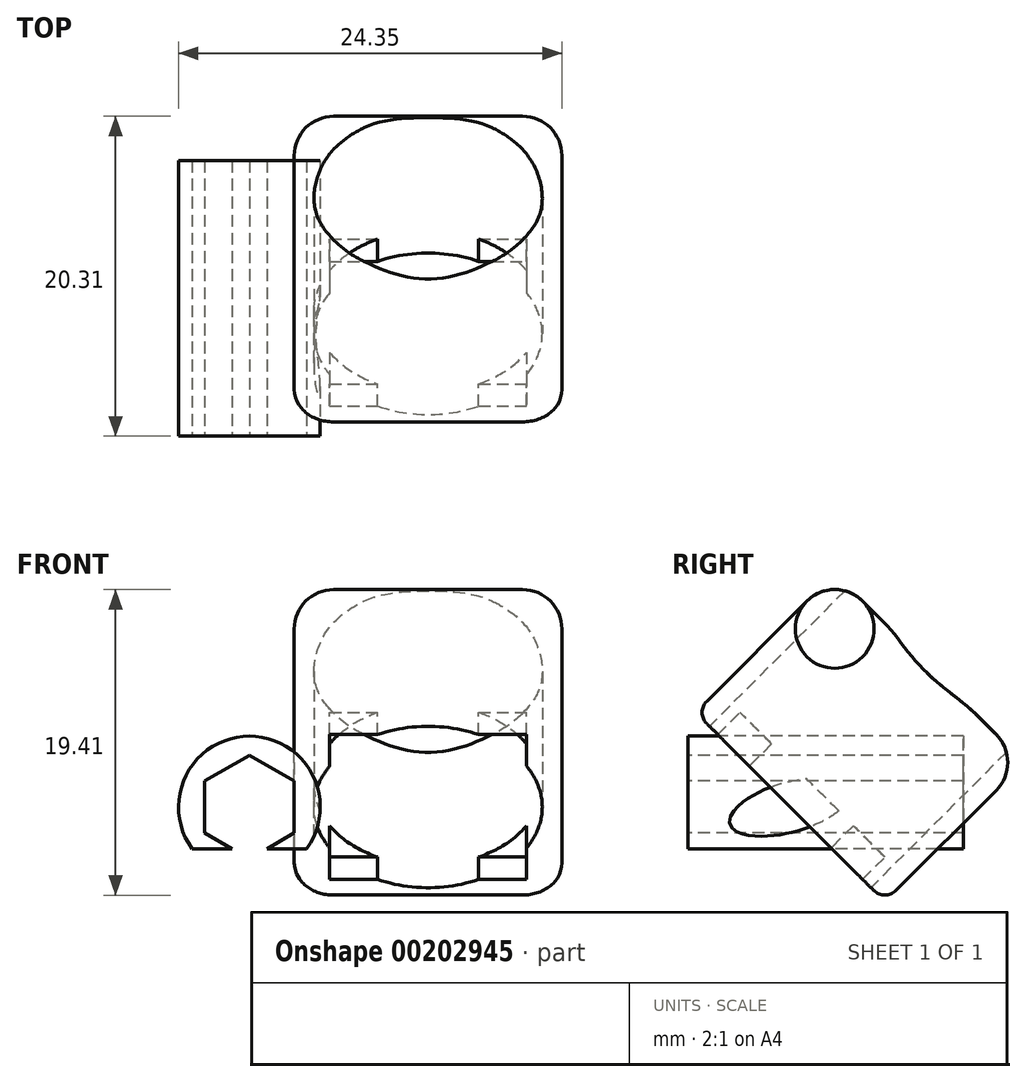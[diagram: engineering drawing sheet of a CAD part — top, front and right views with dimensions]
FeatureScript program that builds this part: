
annotation { "Feature Type Name" : "Feature", "Feature Type Description" : "" }
export const myFeature = defineFeature(function(context is Context, id is Id, definition is map)
    precondition{}
    {
        {
            var Q0;
            Q0=qCreatedBy(makeId("Top.planeOp"),FACE);
            var sketch = newSketch(context, id + "F0", { "sketchPlane" : qUnion([Q0])});
            skLineSegment(sketch, "E0.bottom", {"start": v(6.25, 6.25) * mm, "end": v(-6.25, 6.25) * mm});
            skLineSegment(sketch, "E0.top", {"start": v(6.25, -6.25) * mm, "end": v(-6.25, -6.25) * mm});
            skLineSegment(sketch, "E0.left", {"start": v(6.25, 6.25) * mm, "end": v(6.25, -6.25) * mm});
            skLineSegment(sketch, "E0.right", {"start": v(-6.25, 6.25) * mm, "end": v(-6.25, -6.25) * mm});
            skPoint(sketch, "E0.middle", {"position": v(0, 0) * mm});
            skCircle(sketch, "E1", {"center": v(0, 0) * mm, "radius": 7.25 * mm});
            skLineSegment(sketch, "E2.bottom", {"start": v(8.5, 8.5) * mm, "end": v(-8.5, 8.5) * mm});
            skLineSegment(sketch, "E2.top", {"start": v(8.5, -8.5) * mm, "end": v(-8.5, -8.5) * mm});
            skLineSegment(sketch, "E2.left", {"start": v(8.5, 8.5) * mm, "end": v(8.5, -8.5) * mm});
            skLineSegment(sketch, "E2.right", {"start": v(-8.5, 8.5) * mm, "end": v(-8.5, -8.5) * mm});
            skSolve(sketch);
        }
        {
            var Q0;
            Q0=makeQuery(id+"F0.imprint","IMPRINT",FACE,{"disambiguationData":[TD([[makeQuery(id+"F0.imprint","IMPRINT",EDGE,{"derivedFrom":sQuery(id+"F0.wireOp",EDGE,"E2.bottom")}),1.0]])]});
            var Q1;
            {var subQ0=sQuery(id+"F0.wireOp",EDGE,"E0.right");var subQ1=sQuery(id+"F0.wireOp",EDGE,"E0.bottom");var subQ2=makeQuery(id+"F0.imprint","INTERSECT",VERTEX,{"derivedFrom":[subQ1,subQ0]});Q1=makeQuery(id+"F0.imprint","IMPRINT",FACE,{"disambiguationData":[TD([[makeQuery(id+"F0.imprint","IMPRINT",EDGE,{"disambiguationData":[TD([[subQ2,1.0]])],"derivedFrom":subQ1}),1.0]])]});}
            var Q2;
            {var subQ0=sQuery(id+"F0.wireOp",EDGE,"E1");var subQ1=makeQuery(id+"F0.imprint","INTERSECT",VERTEX,{"derivedFrom":[sQuery(id+"F0.wireOp",EDGE,"E0.bottom"),subQ0]});Q2=makeQuery(id+"F0.imprint","IMPRINT",FACE,{"disambiguationData":[TD([[makeQuery(id+"F0.imprint","IMPRINT",EDGE,{"disambiguationData":[TD([[subQ1,1.0]])],"derivedFrom":subQ0}),1.0]])]});}
            var Q3;
            {var subQ0=sQuery(id+"F0.wireOp",EDGE,"E0.left");var subQ1=sQuery(id+"F0.wireOp",EDGE,"E0.bottom");var subQ2=makeQuery(id+"F0.imprint","INTERSECT",VERTEX,{"derivedFrom":[subQ1,subQ0]});Q3=makeQuery(id+"F0.imprint","IMPRINT",FACE,{"disambiguationData":[TD([[makeQuery(id+"F0.imprint","IMPRINT",EDGE,{"disambiguationData":[TD([[subQ2,-1.0]])],"derivedFrom":subQ1}),1.0]])]});}
            var Q4;
            {var subQ0=sQuery(id+"F0.wireOp",EDGE,"E0.left");var subQ1=sQuery(id+"F0.wireOp",EDGE,"E0.top");var subQ2=makeQuery(id+"F0.imprint","INTERSECT",VERTEX,{"derivedFrom":[subQ1,subQ0]});Q4=makeQuery(id+"F0.imprint","IMPRINT",FACE,{"disambiguationData":[TD([[makeQuery(id+"F0.imprint","IMPRINT",EDGE,{"disambiguationData":[TD([[subQ2,-1.0]])],"derivedFrom":subQ1}),-1.0]])]});}
            var Q5;
            {var subQ0=sQuery(id+"F0.wireOp",EDGE,"E0.right");var subQ1=sQuery(id+"F0.wireOp",EDGE,"E0.top");var subQ2=makeQuery(id+"F0.imprint","INTERSECT",VERTEX,{"derivedFrom":[subQ1,subQ0]});Q5=makeQuery(id+"F0.imprint","IMPRINT",FACE,{"disambiguationData":[TD([[makeQuery(id+"F0.imprint","IMPRINT",EDGE,{"disambiguationData":[TD([[subQ2,1.0]])],"derivedFrom":subQ1}),-1.0]])]});}
            extrude(context, id + "F1", {"entities" : qUnion([Q0, Q1, Q2, Q3, Q4, Q5]), "depth" : 12.5 * mm});
        }
        {
            var Q0;
            Q0=qCreatedBy(makeId("Top.planeOp"),FACE);
            var sketch = newSketch(context, id + "F2", { "sketchPlane" : qUnion([Q0])});
            skLineSegment(sketch, "E3", {"start": v(-15.14, 0) * mm, "end": v(14.33, 0) * mm});
            skSolve(sketch);
        }
        {
            var Q0;
            Q0=qCreatedBy(makeId("Front.planeOp"),FACE);
            var sketch = newSketch(context, id + "F3", { "sketchPlane" : qUnion([Q0])});
            skCircle(sketch, "E4", {"center": v(-11.35, 0) * mm, "radius": 4.5 * mm});
            skCircle(sketch, "E5.cCircle", {"center": v(-11.35, 0) * mm, "radius": 2.85 * mm, "construction": true});
            skLineSegment(sketch, "E5.0", {"start": v(-8.5, 1.65) * mm, "end": v(-8.5, -1.65) * mm});
            skLineSegment(sketch, "E5.1", {"start": v(-8.5, -1.65) * mm, "end": v(-11.35, -3.3) * mm});
            skLineSegment(sketch, "E5.2", {"start": v(-11.35, -3.3) * mm, "end": v(-14.2, -1.65) * mm});
            skLineSegment(sketch, "E5.3", {"start": v(-14.2, -1.65) * mm, "end": v(-14.2, 1.65) * mm});
            skLineSegment(sketch, "E5.4", {"start": v(-14.2, 1.65) * mm, "end": v(-11.35, 3.3) * mm});
            skLineSegment(sketch, "E5.5", {"start": v(-11.35, 3.3) * mm, "end": v(-8.5, 1.65) * mm});
            skPoint(sketch, "E5.0.midPoint", {"position": v(-8.5, 0) * mm});
            skPoint(sketch, "E6.visualSharp", {"position": v(20, -23.1) * mm});
            skArc(sketch, "E7", {"start": v(3.92, -36.51) * mm, "mid": v(1.52, -37.5) * mm, "end": v(0.52, -39.91) * mm});
            skArc(sketch, "E8", {"start": v(0.52, -39.91) * mm, "mid": v(1.52, -42.32) * mm, "end": v(3.92, -43.31) * mm});
            skArc(sketch, "E9", {"start": v(3.92, -43.31) * mm, "mid": v(6.32, -42.32) * mm, "end": v(7.32, -39.91) * mm});
            skArc(sketch, "E10", {"start": v(7.32, -39.91) * mm, "mid": v(6.32, -37.5) * mm, "end": v(3.92, -36.51) * mm});
            skLineSegment(sketch, "E11", {"start": v(13.47, -32.4) * mm, "end": v(14.37, -29.02) * mm});
            skArc(sketch, "E12", {"start": v(14.37, -29.02) * mm, "mid": v(14.86, -28.38) * mm, "end": v(15.66, -28.28) * mm});
            skArc(sketch, "E13", {"start": v(15.66, -28.28) * mm, "mid": v(16.3, -28.77) * mm, "end": v(16.4, -29.56) * mm});
            skLineSegment(sketch, "E14", {"start": v(16.4, -29.56) * mm, "end": v(15.5, -32.94) * mm});
            skArc(sketch, "E15", {"start": v(15.5, -32.94) * mm, "mid": v(15, -33.58) * mm, "end": v(14.2, -33.69) * mm});
            skArc(sketch, "E16", {"start": v(14.2, -33.69) * mm, "mid": v(13.57, -33.2) * mm, "end": v(13.47, -32.4) * mm});
            skLineSegment(sketch, "E17", {"start": v(4.42, -34.66) * mm, "end": v(4.44, -34.66) * mm});
            skArc(sketch, "E18", {"start": v(4.44, -34.66) * mm, "mid": v(5.22, -34.2) * mm, "end": v(5.2, -33.28) * mm});
            skLineSegment(sketch, "E19", {"start": v(5.2, -33.28) * mm, "end": v(4.72, -32.52) * mm});
            skLineSegment(sketch, "E20", {"start": v(4.72, -32.52) * mm, "end": v(4.37, -31.96) * mm});
            skLineSegment(sketch, "E21", {"start": v(4.37, -31.96) * mm, "end": v(4.37, -31.94) * mm});
            skLineSegment(sketch, "E22", {"start": v(4.37, -31.94) * mm, "end": v(4.6, -31.62) * mm});
            skLineSegment(sketch, "E23", {"start": v(4.6, -31.62) * mm, "end": v(4.94, -31.07) * mm});
            skLineSegment(sketch, "E24", {"start": v(4.94, -31.07) * mm, "end": v(5.24, -30.47) * mm});
            skLineSegment(sketch, "E25", {"start": v(5.24, -30.47) * mm, "end": v(5.32, -30.27) * mm});
            skLineSegment(sketch, "E26", {"start": v(5.32, -30.27) * mm, "end": v(5.34, -30.22) * mm});
            skLineSegment(sketch, "E27", {"start": v(5.34, -30.22) * mm, "end": v(5.36, -30.18) * mm});
            skLineSegment(sketch, "E28", {"start": v(5.36, -30.18) * mm, "end": v(5.5, -29.83) * mm});
            skLineSegment(sketch, "E29", {"start": v(5.5, -29.83) * mm, "end": v(5.61, -29.45) * mm});
            skLineSegment(sketch, "E30", {"start": v(5.61, -29.45) * mm, "end": v(5.72, -29.07) * mm});
            skLineSegment(sketch, "E31", {"start": v(5.72, -29.07) * mm, "end": v(5.8, -28.68) * mm});
            skLineSegment(sketch, "E32", {"start": v(5.8, -28.68) * mm, "end": v(5.87, -28.28) * mm});
            skLineSegment(sketch, "E33", {"start": v(5.87, -28.28) * mm, "end": v(5.92, -27.87) * mm});
            skLineSegment(sketch, "E34", {"start": v(5.92, -27.87) * mm, "end": v(5.95, -27.45) * mm});
            skLineSegment(sketch, "E35", {"start": v(5.95, -27.45) * mm, "end": v(5.96, -27.03) * mm});
            skLineSegment(sketch, "E36", {"start": v(5.96, -27.03) * mm, "end": v(5.95, -26.6) * mm});
            skLineSegment(sketch, "E37", {"start": v(5.95, -26.6) * mm, "end": v(5.92, -26.2) * mm});
            skLineSegment(sketch, "E38", {"start": v(5.92, -26.2) * mm, "end": v(5.87, -25.79) * mm});
            skLineSegment(sketch, "E39", {"start": v(5.87, -25.79) * mm, "end": v(5.8, -25.39) * mm});
            skLineSegment(sketch, "E40", {"start": v(5.8, -25.39) * mm, "end": v(5.72, -25) * mm});
            skLineSegment(sketch, "E41", {"start": v(5.72, -25) * mm, "end": v(5.61, -24.61) * mm});
            skLineSegment(sketch, "E42", {"start": v(5.61, -24.61) * mm, "end": v(5.5, -24.24) * mm});
            skLineSegment(sketch, "E43", {"start": v(5.5, -24.24) * mm, "end": v(5.36, -23.88) * mm});
            skLineSegment(sketch, "E44", {"start": v(5.36, -23.88) * mm, "end": v(5.34, -23.84) * mm});
            skLineSegment(sketch, "E45", {"start": v(5.34, -23.84) * mm, "end": v(5.32, -23.8) * mm});
            skLineSegment(sketch, "E46", {"start": v(5.32, -23.8) * mm, "end": v(5.24, -23.6) * mm});
            skLineSegment(sketch, "E47", {"start": v(5.24, -23.6) * mm, "end": v(4.94, -23) * mm});
            skLineSegment(sketch, "E48", {"start": v(4.94, -23) * mm, "end": v(4.6, -22.44) * mm});
            skLineSegment(sketch, "E49", {"start": v(4.6, -22.44) * mm, "end": v(4.37, -22.12) * mm});
            skLineSegment(sketch, "E50", {"start": v(4.37, -22.12) * mm, "end": v(4.37, -22.1) * mm});
            skLineSegment(sketch, "E51", {"start": v(4.37, -22.1) * mm, "end": v(4.72, -21.54) * mm});
            skLineSegment(sketch, "E52", {"start": v(4.72, -21.54) * mm, "end": v(5.2, -20.78) * mm});
            skArc(sketch, "E53", {"start": v(5.2, -20.78) * mm, "mid": v(5.22, -19.87) * mm, "end": v(4.44, -19.4) * mm});
            skLineSegment(sketch, "E54", {"start": v(4.44, -19.4) * mm, "end": v(3.9, -19.4) * mm});
            skArc(sketch, "E55", {"start": v(3.9, -19.4) * mm, "mid": v(3.47, -19.52) * mm, "end": v(3.15, -19.82) * mm});
            skLineSegment(sketch, "E56", {"start": v(3.15, -19.82) * mm, "end": v(2.68, -20.58) * mm});
            skLineSegment(sketch, "E57", {"start": v(2.68, -20.58) * mm, "end": v(2.37, -20.4) * mm});
            skLineSegment(sketch, "E58", {"start": v(2.37, -20.4) * mm, "end": v(2.06, -20.25) * mm});
            skLineSegment(sketch, "E59", {"start": v(2.06, -20.25) * mm, "end": v(1.74, -20.12) * mm});
            skLineSegment(sketch, "E60", {"start": v(1.74, -20.12) * mm, "end": v(1.41, -20.01) * mm});
            skLineSegment(sketch, "E61", {"start": v(1.41, -20.01) * mm, "end": v(1.08, -19.93) * mm});
            skLineSegment(sketch, "E62", {"start": v(1.08, -19.93) * mm, "end": v(0.73, -19.86) * mm});
            skLineSegment(sketch, "E63", {"start": v(0.73, -19.86) * mm, "end": v(0.38, -19.83) * mm});
            skLineSegment(sketch, "E64", {"start": v(0.38, -19.83) * mm, "end": v(0.03, -19.81) * mm});
            skLineSegment(sketch, "E65", {"start": v(0.03, -19.81) * mm, "end": v(-0.04, -19.82) * mm});
            skLineSegment(sketch, "E66", {"start": v(-0.04, -19.82) * mm, "end": v(-0.11, -19.81) * mm});
            skLineSegment(sketch, "E67", {"start": v(-0.11, -19.81) * mm, "end": v(-0.46, -19.83) * mm});
            skLineSegment(sketch, "E68", {"start": v(-0.46, -19.83) * mm, "end": v(-0.8, -19.86) * mm});
            skLineSegment(sketch, "E69", {"start": v(-0.8, -19.86) * mm, "end": v(-1.15, -19.92) * mm});
            skLineSegment(sketch, "E70", {"start": v(-1.15, -19.92) * mm, "end": v(-1.48, -20) * mm});
            skLineSegment(sketch, "E71", {"start": v(-1.48, -20) * mm, "end": v(-1.8, -20.11) * mm});
            skLineSegment(sketch, "E72", {"start": v(-1.8, -20.11) * mm, "end": v(-2.12, -20.24) * mm});
            skLineSegment(sketch, "E73", {"start": v(-2.12, -20.24) * mm, "end": v(-2.43, -20.39) * mm});
            skLineSegment(sketch, "E74", {"start": v(-2.43, -20.39) * mm, "end": v(-2.73, -20.56) * mm});
            skLineSegment(sketch, "E75", {"start": v(-2.73, -20.56) * mm, "end": v(-2.98, -20.21) * mm});
            skLineSegment(sketch, "E76", {"start": v(-2.98, -20.21) * mm, "end": v(-3.05, -20.11) * mm});
            skLineSegment(sketch, "E77", {"start": v(-3.05, -20.11) * mm, "end": v(-3.24, -19.82) * mm});
            skArc(sketch, "E78", {"start": v(-3.24, -19.82) * mm, "mid": v(-3.56, -19.52) * mm, "end": v(-4, -19.4) * mm});
            skLineSegment(sketch, "E79", {"start": v(-4, -19.4) * mm, "end": v(-4.52, -19.4) * mm});
            skArc(sketch, "E80", {"start": v(-4.52, -19.4) * mm, "mid": v(-5.31, -19.87) * mm, "end": v(-5.29, -20.78) * mm});
            skLineSegment(sketch, "E81", {"start": v(-5.29, -20.78) * mm, "end": v(-4.45, -22.11) * mm});
            skLineSegment(sketch, "E82", {"start": v(-4.45, -22.11) * mm, "end": v(-4.63, -22.36) * mm});
            skLineSegment(sketch, "E83", {"start": v(-4.63, -22.36) * mm, "end": v(-4.8, -22.61) * mm});
            skLineSegment(sketch, "E84", {"start": v(-4.8, -22.61) * mm, "end": v(-4.96, -22.88) * mm});
            skLineSegment(sketch, "E85", {"start": v(-4.96, -22.88) * mm, "end": v(-5.12, -23.16) * mm});
            skLineSegment(sketch, "E86", {"start": v(-5.12, -23.16) * mm, "end": v(-5.26, -23.44) * mm});
            skLineSegment(sketch, "E87", {"start": v(-5.26, -23.44) * mm, "end": v(-5.39, -23.73) * mm});
            skLineSegment(sketch, "E88", {"start": v(-5.39, -23.73) * mm, "end": v(-5.5, -24.03) * mm});
            skLineSegment(sketch, "E89", {"start": v(-5.5, -24.03) * mm, "end": v(-5.62, -24.34) * mm});
            skLineSegment(sketch, "E90", {"start": v(-5.62, -24.34) * mm, "end": v(-5.71, -24.66) * mm});
            skLineSegment(sketch, "E91", {"start": v(-5.71, -24.66) * mm, "end": v(-5.8, -24.98) * mm});
            skLineSegment(sketch, "E92", {"start": v(-5.8, -24.98) * mm, "end": v(-5.87, -25.3) * mm});
            skLineSegment(sketch, "E93", {"start": v(-5.87, -25.3) * mm, "end": v(-5.93, -25.64) * mm});
            skLineSegment(sketch, "E94", {"start": v(-5.93, -25.64) * mm, "end": v(-5.98, -25.98) * mm});
            skLineSegment(sketch, "E95", {"start": v(-5.98, -25.98) * mm, "end": v(-6.02, -26.33) * mm});
            skLineSegment(sketch, "E96", {"start": v(-6.02, -26.33) * mm, "end": v(-6.04, -26.68) * mm});
            skLineSegment(sketch, "E97", {"start": v(-6.04, -26.68) * mm, "end": v(-6.04, -27.03) * mm});
            skLineSegment(sketch, "E98", {"start": v(-6.04, -27.03) * mm, "end": v(-6.04, -27.39) * mm});
            skLineSegment(sketch, "E99", {"start": v(-6.04, -27.39) * mm, "end": v(-6.02, -27.74) * mm});
            skLineSegment(sketch, "E100", {"start": v(-6.02, -27.74) * mm, "end": v(-5.98, -28.08) * mm});
            skLineSegment(sketch, "E101", {"start": v(-5.98, -28.08) * mm, "end": v(-5.93, -28.42) * mm});
            skLineSegment(sketch, "E102", {"start": v(-5.93, -28.42) * mm, "end": v(-5.87, -28.76) * mm});
            skLineSegment(sketch, "E103", {"start": v(-5.87, -28.76) * mm, "end": v(-5.8, -29.08) * mm});
            skLineSegment(sketch, "E104", {"start": v(-5.8, -29.08) * mm, "end": v(-5.71, -29.4) * mm});
            skLineSegment(sketch, "E105", {"start": v(-5.71, -29.4) * mm, "end": v(-5.62, -29.72) * mm});
            skLineSegment(sketch, "E106", {"start": v(-5.62, -29.72) * mm, "end": v(-5.5, -30.03) * mm});
            skLineSegment(sketch, "E107", {"start": v(-5.5, -30.03) * mm, "end": v(-5.39, -30.33) * mm});
            skLineSegment(sketch, "E108", {"start": v(-5.39, -30.33) * mm, "end": v(-5.26, -30.62) * mm});
            skLineSegment(sketch, "E109", {"start": v(-5.26, -30.62) * mm, "end": v(-5.12, -30.9) * mm});
            skLineSegment(sketch, "E110", {"start": v(-5.12, -30.9) * mm, "end": v(-4.96, -31.18) * mm});
            skLineSegment(sketch, "E111", {"start": v(-4.96, -31.18) * mm, "end": v(-4.8, -31.45) * mm});
            skLineSegment(sketch, "E112", {"start": v(-4.8, -31.45) * mm, "end": v(-4.63, -31.7) * mm});
            skLineSegment(sketch, "E113", {"start": v(-4.63, -31.7) * mm, "end": v(-4.45, -31.95) * mm});
            skLineSegment(sketch, "E114", {"start": v(-4.45, -31.95) * mm, "end": v(-5.29, -33.28) * mm});
            skArc(sketch, "E115", {"start": v(-5.29, -33.28) * mm, "mid": v(-5.31, -34.2) * mm, "end": v(-4.52, -34.66) * mm});
            skLineSegment(sketch, "E116", {"start": v(-4.52, -34.66) * mm, "end": v(-4.44, -34.66) * mm});
            skLineSegment(sketch, "E117", {"start": v(-4.44, -34.66) * mm, "end": v(-4.36, -34.66) * mm});
            skLineSegment(sketch, "E118", {"start": v(-4.36, -34.66) * mm, "end": v(-4, -34.66) * mm});
            skArc(sketch, "E119", {"start": v(-4, -34.66) * mm, "mid": v(-3.56, -34.55) * mm, "end": v(-3.24, -34.24) * mm});
            skLineSegment(sketch, "E120", {"start": v(-3.24, -34.24) * mm, "end": v(-3.05, -33.95) * mm});
            skLineSegment(sketch, "E121", {"start": v(-3.05, -33.95) * mm, "end": v(-2.98, -33.85) * mm});
            skLineSegment(sketch, "E122", {"start": v(-2.98, -33.85) * mm, "end": v(-2.73, -33.5) * mm});
            skLineSegment(sketch, "E123", {"start": v(-2.73, -33.5) * mm, "end": v(-2.43, -33.68) * mm});
            skLineSegment(sketch, "E124", {"start": v(-2.43, -33.68) * mm, "end": v(-2.12, -33.82) * mm});
            skLineSegment(sketch, "E125", {"start": v(-2.12, -33.82) * mm, "end": v(-1.8, -33.95) * mm});
            skLineSegment(sketch, "E126", {"start": v(-1.8, -33.95) * mm, "end": v(-1.48, -34.06) * mm});
            skLineSegment(sketch, "E127", {"start": v(-1.48, -34.06) * mm, "end": v(-1.15, -34.14) * mm});
            skLineSegment(sketch, "E128", {"start": v(-1.15, -34.14) * mm, "end": v(-0.8, -34.2) * mm});
            skLineSegment(sketch, "E129", {"start": v(-0.8, -34.2) * mm, "end": v(-0.46, -34.24) * mm});
            skLineSegment(sketch, "E130", {"start": v(-0.46, -34.24) * mm, "end": v(-0.11, -34.25) * mm});
            skLineSegment(sketch, "E131", {"start": v(-0.11, -34.25) * mm, "end": v(-0.06, -34.25) * mm});
            skLineSegment(sketch, "E132", {"start": v(-0.06, -34.25) * mm, "end": v(0.03, -34.25) * mm});
            skLineSegment(sketch, "E133", {"start": v(0.03, -34.25) * mm, "end": v(0.38, -34.24) * mm});
            skLineSegment(sketch, "E134", {"start": v(0.38, -34.24) * mm, "end": v(0.73, -34.2) * mm});
            skLineSegment(sketch, "E135", {"start": v(0.73, -34.2) * mm, "end": v(1.08, -34.14) * mm});
            skLineSegment(sketch, "E136", {"start": v(1.08, -34.14) * mm, "end": v(1.41, -34.05) * mm});
            skLineSegment(sketch, "E137", {"start": v(1.41, -34.05) * mm, "end": v(1.74, -33.94) * mm});
            skLineSegment(sketch, "E138", {"start": v(1.74, -33.94) * mm, "end": v(2.06, -33.8) * mm});
            skLineSegment(sketch, "E139", {"start": v(2.06, -33.8) * mm, "end": v(2.37, -33.66) * mm});
            skLineSegment(sketch, "E140", {"start": v(2.37, -33.66) * mm, "end": v(2.68, -33.48) * mm});
            skLineSegment(sketch, "E141", {"start": v(2.68, -33.48) * mm, "end": v(3.15, -34.24) * mm});
            skArc(sketch, "E142", {"start": v(3.15, -34.24) * mm, "mid": v(3.47, -34.55) * mm, "end": v(3.9, -34.66) * mm});
            skLineSegment(sketch, "E143", {"start": v(3.9, -34.66) * mm, "end": v(4.42, -34.66) * mm});
            skLineSegment(sketch, "E144", {"start": v(-13.55, -32.4) * mm, "end": v(-14.46, -29.02) * mm});
            skArc(sketch, "E145", {"start": v(-14.46, -29.02) * mm, "mid": v(-14.95, -28.38) * mm, "end": v(-15.75, -28.28) * mm});
            skArc(sketch, "E146", {"start": v(-15.75, -28.28) * mm, "mid": v(-16.38, -28.77) * mm, "end": v(-16.49, -29.56) * mm});
            skLineSegment(sketch, "E147", {"start": v(-16.49, -29.56) * mm, "end": v(-15.58, -32.94) * mm});
            skArc(sketch, "E148", {"start": v(-15.58, -32.94) * mm, "mid": v(-15.1, -33.58) * mm, "end": v(-14.3, -33.69) * mm});
            skArc(sketch, "E149", {"start": v(-14.3, -33.69) * mm, "mid": v(-13.66, -33.2) * mm, "end": v(-13.55, -32.4) * mm});
            skLineSegment(sketch, "E150", {"start": v(15.57, 0.36) * mm, "end": v(15.63, 0.26) * mm});
            skLineSegment(sketch, "E151", {"start": v(15.66, 0.2) * mm, "end": v(16.02, -0.48) * mm});
            skLineSegment(sketch, "E152", {"start": v(16.05, -0.53) * mm, "end": v(16.4, -1.23) * mm});
            skLineSegment(sketch, "E153", {"start": v(16.42, -1.28) * mm, "end": v(16.74, -2) * mm});
            skLineSegment(sketch, "E154", {"start": v(16.76, -2.04) * mm, "end": v(17.06, -2.76) * mm});
            skLineSegment(sketch, "E155", {"start": v(17.08, -2.8) * mm, "end": v(17.37, -3.53) * mm});
            skLineSegment(sketch, "E156", {"start": v(17.38, -3.58) * mm, "end": v(17.65, -4.3) * mm});
            skLineSegment(sketch, "E157", {"start": v(17.66, -4.35) * mm, "end": v(17.9, -5.1) * mm});
            skLineSegment(sketch, "E158", {"start": v(17.92, -5.13) * mm, "end": v(18.15, -5.88) * mm});
            skLineSegment(sketch, "E159", {"start": v(18.16, -5.92) * mm, "end": v(18.37, -6.67) * mm});
            skLineSegment(sketch, "E160", {"start": v(18.38, -6.7) * mm, "end": v(18.58, -7.46) * mm});
            skLineSegment(sketch, "E161", {"start": v(18.59, -7.5) * mm, "end": v(18.77, -8.25) * mm});
            skLineSegment(sketch, "E162", {"start": v(18.78, -8.28) * mm, "end": v(18.94, -9.04) * mm});
            skLineSegment(sketch, "E163", {"start": v(18.95, -9.07) * mm, "end": v(19.1, -9.83) * mm});
            skLineSegment(sketch, "E164", {"start": v(19.1, -9.86) * mm, "end": v(19.24, -10.62) * mm});
            skLineSegment(sketch, "E165", {"start": v(19.24, -10.65) * mm, "end": v(19.37, -11.4) * mm});
            skLineSegment(sketch, "E166", {"start": v(19.37, -11.44) * mm, "end": v(19.48, -12.2) * mm});
            skLineSegment(sketch, "E167", {"start": v(19.48, -12.22) * mm, "end": v(19.58, -12.98) * mm});
            skLineSegment(sketch, "E168", {"start": v(19.58, -13) * mm, "end": v(19.67, -13.76) * mm});
            skLineSegment(sketch, "E169", {"start": v(19.67, -13.78) * mm, "end": v(19.74, -14.53) * mm});
            skLineSegment(sketch, "E170", {"start": v(19.75, -14.56) * mm, "end": v(19.81, -15.3) * mm});
            skLineSegment(sketch, "E171", {"start": v(19.81, -15.32) * mm, "end": v(19.87, -16.06) * mm});
            skLineSegment(sketch, "E172", {"start": v(19.87, -16.08) * mm, "end": v(19.91, -16.81) * mm});
            skLineSegment(sketch, "E173", {"start": v(19.91, -16.84) * mm, "end": v(19.95, -17.56) * mm});
            skLineSegment(sketch, "E174", {"start": v(19.95, -17.6) * mm, "end": v(20, -19.02) * mm});
            skLineSegment(sketch, "E175", {"start": v(20, -19.05) * mm, "end": v(20.02, -20.45) * mm});
            skLineSegment(sketch, "E176", {"start": v(20.02, -20.48) * mm, "end": v(20.02, -21.83) * mm});
            skLineSegment(sketch, "E177", {"start": v(20.02, -21.86) * mm, "end": v(20, -23.02) * mm});
            skLineSegment(sketch, "E178", {"start": v(20, -23.05) * mm, "end": v(19.95, -24.25) * mm});
            skLineSegment(sketch, "E179", {"start": v(19.95, -24.29) * mm, "end": v(19.88, -25.51) * mm});
            skLineSegment(sketch, "E180", {"start": v(19.88, -25.55) * mm, "end": v(19.83, -26.17) * mm});
            skLineSegment(sketch, "E181", {"start": v(19.83, -26.2) * mm, "end": v(19.77, -26.82) * mm});
            skLineSegment(sketch, "E182", {"start": v(19.77, -26.84) * mm, "end": v(19.7, -27.47) * mm});
            skLineSegment(sketch, "E183", {"start": v(19.7, -27.5) * mm, "end": v(19.64, -28.14) * mm});
            skLineSegment(sketch, "E184", {"start": v(19.63, -28.16) * mm, "end": v(19.55, -28.8) * mm});
            skLineSegment(sketch, "E185", {"start": v(19.55, -28.83) * mm, "end": v(19.46, -29.47) * mm});
            skLineSegment(sketch, "E186", {"start": v(19.45, -29.5) * mm, "end": v(19.35, -30.15) * mm});
            skLineSegment(sketch, "E187", {"start": v(19.35, -30.18) * mm, "end": v(19.24, -30.82) * mm});
            skLineSegment(sketch, "E188", {"start": v(19.23, -30.85) * mm, "end": v(19.1, -31.5) * mm});
            skLineSegment(sketch, "E189", {"start": v(19.1, -31.53) * mm, "end": v(18.97, -32.18) * mm});
            skLineSegment(sketch, "E190", {"start": v(18.96, -32.22) * mm, "end": v(18.81, -32.86) * mm});
            skLineSegment(sketch, "E191", {"start": v(18.8, -32.9) * mm, "end": v(18.65, -33.54) * mm});
            skLineSegment(sketch, "E192", {"start": v(18.64, -33.58) * mm, "end": v(18.47, -34.23) * mm});
            skLineSegment(sketch, "E193", {"start": v(18.46, -34.26) * mm, "end": v(18.27, -34.9) * mm});
            skLineSegment(sketch, "E194", {"start": v(18.26, -34.94) * mm, "end": v(18.06, -35.58) * mm});
            skLineSegment(sketch, "E195", {"start": v(18.05, -35.62) * mm, "end": v(17.83, -36.26) * mm});
            skLineSegment(sketch, "E196", {"start": v(17.82, -36.3) * mm, "end": v(17.6, -36.93) * mm});
            skLineSegment(sketch, "E197", {"start": v(17.57, -36.97) * mm, "end": v(17.33, -37.6) * mm});
            skLineSegment(sketch, "E198", {"start": v(17.31, -37.64) * mm, "end": v(17.05, -38.27) * mm});
            skLineSegment(sketch, "E199", {"start": v(17.04, -38.31) * mm, "end": v(16.76, -38.93) * mm});
            skLineSegment(sketch, "E200", {"start": v(16.74, -38.97) * mm, "end": v(16.45, -39.58) * mm});
            skLineSegment(sketch, "E201", {"start": v(16.42, -39.63) * mm, "end": v(16.11, -40.23) * mm});
            skLineSegment(sketch, "E202", {"start": v(16.09, -40.27) * mm, "end": v(15.76, -40.87) * mm});
            skLineSegment(sketch, "E203", {"start": v(15.73, -40.92) * mm, "end": v(15.48, -41.35) * mm});
            skLineSegment(sketch, "E204", {"start": v(8.6, -44.86) * mm, "end": v(2.96, -44.86) * mm});
            skLineSegment(sketch, "E205", {"start": v(2.96, -44.86) * mm, "end": v(-0.04, -44.86) * mm});
            skLineSegment(sketch, "E206", {"start": v(-0.04, -44.86) * mm, "end": v(-3.04, -44.86) * mm});
            skLineSegment(sketch, "E207", {"start": v(-3.04, -44.86) * mm, "end": v(-8.6, -44.86) * mm});
            skLineSegment(sketch, "E208", {"start": v(-15.74, -40.47) * mm, "end": v(-16.08, -39.89) * mm});
            skLineSegment(sketch, "E209", {"start": v(-16.08, -39.89) * mm, "end": v(-16.41, -39.3) * mm});
            skLineSegment(sketch, "E210", {"start": v(-16.41, -39.3) * mm, "end": v(-16.72, -38.7) * mm});
            skLineSegment(sketch, "E211", {"start": v(-16.72, -38.7) * mm, "end": v(-17.01, -38.09) * mm});
            skLineSegment(sketch, "E212", {"start": v(-17.01, -38.09) * mm, "end": v(-17.29, -37.47) * mm});
            skLineSegment(sketch, "E213", {"start": v(-17.29, -37.47) * mm, "end": v(-17.55, -36.85) * mm});
            skLineSegment(sketch, "E214", {"start": v(-17.55, -36.85) * mm, "end": v(-17.79, -36.22) * mm});
            skLineSegment(sketch, "E215", {"start": v(-17.79, -36.22) * mm, "end": v(-18.02, -35.6) * mm});
            skLineSegment(sketch, "E216", {"start": v(-18.02, -35.6) * mm, "end": v(-18.23, -34.96) * mm});
            skLineSegment(sketch, "E217", {"start": v(-18.23, -34.96) * mm, "end": v(-18.43, -34.32) * mm});
            skLineSegment(sketch, "E218", {"start": v(-18.43, -34.32) * mm, "end": v(-18.61, -33.67) * mm});
            skLineSegment(sketch, "E219", {"start": v(-18.61, -33.67) * mm, "end": v(-18.79, -33.03) * mm});
            skLineSegment(sketch, "E220", {"start": v(-18.79, -33.03) * mm, "end": v(-18.95, -32.38) * mm});
            skLineSegment(sketch, "E221", {"start": v(-18.95, -32.38) * mm, "end": v(-19.1, -31.73) * mm});
            skLineSegment(sketch, "E222", {"start": v(-19.1, -31.73) * mm, "end": v(-19.23, -31.09) * mm});
            skLineSegment(sketch, "E223", {"start": v(-19.23, -31.09) * mm, "end": v(-19.35, -30.44) * mm});
            skLineSegment(sketch, "E224", {"start": v(-19.35, -30.44) * mm, "end": v(-19.46, -29.8) * mm});
            skLineSegment(sketch, "E225", {"start": v(-19.46, -29.8) * mm, "end": v(-19.56, -29.15) * mm});
            skLineSegment(sketch, "E226", {"start": v(-19.56, -29.15) * mm, "end": v(-19.65, -28.5) * mm});
            skLineSegment(sketch, "E227", {"start": v(-19.65, -28.5) * mm, "end": v(-19.73, -27.86) * mm});
            skLineSegment(sketch, "E228", {"start": v(-19.73, -27.86) * mm, "end": v(-19.8, -27.22) * mm});
            skLineSegment(sketch, "E229", {"start": v(-19.8, -27.22) * mm, "end": v(-19.87, -26.6) * mm});
            skLineSegment(sketch, "E230", {"start": v(-19.87, -26.6) * mm, "end": v(-19.97, -25.34) * mm});
            skLineSegment(sketch, "E231", {"start": v(-19.97, -25.34) * mm, "end": v(-20.04, -24.12) * mm});
            skLineSegment(sketch, "E232", {"start": v(-20.04, -24.12) * mm, "end": v(-20.08, -22.92) * mm});
            skLineSegment(sketch, "E233", {"start": v(-20.08, -22.92) * mm, "end": v(-20.1, -21.76) * mm});
            skLineSegment(sketch, "E234", {"start": v(-20.1, -21.76) * mm, "end": v(-20.1, -20.41) * mm});
            skLineSegment(sketch, "E235", {"start": v(-20.1, -20.41) * mm, "end": v(-20.08, -19.02) * mm});
            skLineSegment(sketch, "E236", {"start": v(-20.08, -19.02) * mm, "end": v(-20.04, -17.6) * mm});
            skLineSegment(sketch, "E237", {"start": v(-20.04, -17.6) * mm, "end": v(-20, -16.87) * mm});
            skLineSegment(sketch, "E238", {"start": v(-20, -16.87) * mm, "end": v(-19.96, -16.13) * mm});
            skLineSegment(sketch, "E239", {"start": v(-19.96, -16.13) * mm, "end": v(-19.9, -15.4) * mm});
            skLineSegment(sketch, "E240", {"start": v(-19.9, -15.4) * mm, "end": v(-19.84, -14.65) * mm});
            skLineSegment(sketch, "E241", {"start": v(-19.84, -14.65) * mm, "end": v(-19.77, -13.9) * mm});
            skLineSegment(sketch, "E242", {"start": v(-19.77, -13.9) * mm, "end": v(-19.68, -13.16) * mm});
            skLineSegment(sketch, "E243", {"start": v(-19.68, -13.16) * mm, "end": v(-19.58, -12.4) * mm});
            skLineSegment(sketch, "E244", {"start": v(-19.58, -12.4) * mm, "end": v(-19.48, -11.65) * mm});
            skLineSegment(sketch, "E245", {"start": v(-19.48, -11.65) * mm, "end": v(-19.35, -10.9) * mm});
            skLineSegment(sketch, "E246", {"start": v(-19.35, -10.9) * mm, "end": v(-19.22, -10.14) * mm});
            skLineSegment(sketch, "E247", {"start": v(-19.22, -10.14) * mm, "end": v(-19.07, -9.38) * mm});
            skLineSegment(sketch, "E248", {"start": v(-19.07, -9.38) * mm, "end": v(-18.9, -8.62) * mm});
            skLineSegment(sketch, "E249", {"start": v(-18.9, -8.62) * mm, "end": v(-18.73, -7.87) * mm});
            skLineSegment(sketch, "E250", {"start": v(-18.73, -7.87) * mm, "end": v(-18.53, -7.12) * mm});
            skLineSegment(sketch, "E251", {"start": v(-18.53, -7.12) * mm, "end": v(-18.32, -6.37) * mm});
            skLineSegment(sketch, "E252", {"start": v(-18.32, -6.37) * mm, "end": v(-18.1, -5.63) * mm});
            skLineSegment(sketch, "E253", {"start": v(-18.1, -5.63) * mm, "end": v(-17.85, -4.9) * mm});
            skLineSegment(sketch, "E254", {"start": v(-17.85, -4.9) * mm, "end": v(-17.58, -4.16) * mm});
            skLineSegment(sketch, "E255", {"start": v(-17.58, -4.16) * mm, "end": v(-17.3, -3.43) * mm});
            skLineSegment(sketch, "E256", {"start": v(-17.3, -3.43) * mm, "end": v(-17, -2.72) * mm});
            skLineSegment(sketch, "E257", {"start": v(-17, -2.72) * mm, "end": v(-16.67, -2) * mm});
            skLineSegment(sketch, "E258", {"start": v(-16.67, -2) * mm, "end": v(-16.33, -1.3) * mm});
            skLineSegment(sketch, "E259", {"start": v(-16.33, -1.3) * mm, "end": v(-15.96, -0.61) * mm});
            skLineSegment(sketch, "E260", {"start": v(-15.96, -0.61) * mm, "end": v(-15.83, -0.39) * mm});
            skArc(sketch, "E261", {"start": v(15.2, -3.8) * mm, "mid": v(16.34, -4.27) * mm, "end": v(16.8, -5.4) * mm});
            skArc(sketch, "E262", {"start": v(16.8, -5.4) * mm, "mid": v(16.34, -6.53) * mm, "end": v(15.2, -7) * mm});
            skArc(sketch, "E263", {"start": v(15.2, -7) * mm, "mid": v(14.08, -6.53) * mm, "end": v(13.6, -5.4) * mm});
            skArc(sketch, "E264", {"start": v(13.6, -5.4) * mm, "mid": v(14.08, -4.27) * mm, "end": v(15.2, -3.8) * mm});
            skArc(sketch, "E265", {"start": v(-15.3, -34.3) * mm, "mid": v(-16.42, -34.77) * mm, "end": v(-16.9, -35.9) * mm});
            skArc(sketch, "E266", {"start": v(-16.9, -35.9) * mm, "mid": v(-16.42, -37.03) * mm, "end": v(-15.3, -37.5) * mm});
            skArc(sketch, "E267", {"start": v(-15.3, -37.5) * mm, "mid": v(-14.16, -37.03) * mm, "end": v(-13.7, -35.9) * mm});
            skArc(sketch, "E268", {"start": v(-13.7, -35.9) * mm, "mid": v(-14.16, -34.77) * mm, "end": v(-15.3, -34.3) * mm});
            skArc(sketch, "E269", {"start": v(15.2, -34.3) * mm, "mid": v(16.34, -34.77) * mm, "end": v(16.8, -35.9) * mm});
            skArc(sketch, "E270", {"start": v(16.8, -35.9) * mm, "mid": v(16.34, -37.03) * mm, "end": v(15.2, -37.5) * mm});
            skArc(sketch, "E271", {"start": v(15.2, -37.5) * mm, "mid": v(14.08, -37.03) * mm, "end": v(13.6, -35.9) * mm});
            skArc(sketch, "E272", {"start": v(13.6, -35.9) * mm, "mid": v(14.08, -34.77) * mm, "end": v(15.2, -34.3) * mm});
            skArc(sketch, "E273", {"start": v(-15.3, -3.8) * mm, "mid": v(-16.42, -4.27) * mm, "end": v(-16.9, -5.4) * mm});
            skArc(sketch, "E274", {"start": v(-16.9, -5.4) * mm, "mid": v(-16.42, -6.53) * mm, "end": v(-15.3, -7) * mm});
            skArc(sketch, "E275", {"start": v(-15.3, -7) * mm, "mid": v(-14.16, -6.53) * mm, "end": v(-13.7, -5.4) * mm});
            skArc(sketch, "E276", {"start": v(-13.7, -5.4) * mm, "mid": v(-14.16, -4.27) * mm, "end": v(-15.3, -3.8) * mm});
            skArc(sketch, "E277", {"start": v(-18.04, -35.65) * mm, "mid": v(-17.16, -37.77) * mm, "end": v(-15.04, -38.65) * mm});
            skLineSegment(sketch, "E278", {"start": v(-15.04, -38.65) * mm, "end": v(14.96, -38.65) * mm});
            skArc(sketch, "E279", {"start": v(14.96, -38.65) * mm, "mid": v(17.08, -37.77) * mm, "end": v(17.96, -35.65) * mm});
            skLineSegment(sketch, "E280", {"start": v(17.96, -35.65) * mm, "end": v(17.96, -5.65) * mm});
            skArc(sketch, "E281", {"start": v(17.96, -5.65) * mm, "mid": v(17.08, -3.53) * mm, "end": v(14.96, -2.65) * mm});
            skLineSegment(sketch, "E282", {"start": v(14.96, -2.65) * mm, "end": v(-15.04, -2.65) * mm});
            skArc(sketch, "E283", {"start": v(-15.04, -2.65) * mm, "mid": v(-17.16, -3.53) * mm, "end": v(-18.04, -5.65) * mm});
            skLineSegment(sketch, "E284", {"start": v(-18.04, -5.65) * mm, "end": v(-18.04, -35.65) * mm});
            skCircle(sketch, "E285.0.1.0", {"center": v(-11.35, -41.3) * mm, "radius": 4.5 * mm});
            skPoint(sketch, "E285.0.1.1", {"position": v(-8.5, -41.3) * mm});
            skCircle(sketch, "E285.0.1.2", {"center": v(-11.35, -41.3) * mm, "radius": 2.85 * mm, "construction": true});
            skLineSegment(sketch, "E285.0.1.3", {"start": v(-8.5, -39.65) * mm, "end": v(-8.5, -42.95) * mm});
            skLineSegment(sketch, "E285.0.1.4", {"start": v(-8.5, -42.95) * mm, "end": v(-11.35, -44.6) * mm});
            skLineSegment(sketch, "E285.0.1.5", {"start": v(-11.35, -44.6) * mm, "end": v(-14.2, -42.95) * mm});
            skLineSegment(sketch, "E285.0.1.6", {"start": v(-14.2, -42.95) * mm, "end": v(-14.2, -39.65) * mm});
            skLineSegment(sketch, "E285.0.1.7", {"start": v(-14.2, -39.65) * mm, "end": v(-11.35, -38) * mm});
            skLineSegment(sketch, "E285.0.1.8", {"start": v(-11.35, -38) * mm, "end": v(-8.5, -39.65) * mm});
            skCircle(sketch, "E285.1.0.0", {"center": v(11.35, 0) * mm, "radius": 4.5 * mm});
            skPoint(sketch, "E285.1.0.1", {"position": v(14.2, 0) * mm});
            skCircle(sketch, "E285.1.0.2", {"center": v(11.35, 0) * mm, "radius": 2.85 * mm, "construction": true});
            skLineSegment(sketch, "E285.1.0.3", {"start": v(14.2, 1.65) * mm, "end": v(14.2, -1.65) * mm});
            skLineSegment(sketch, "E285.1.0.4", {"start": v(14.2, -1.65) * mm, "end": v(11.35, -3.3) * mm});
            skLineSegment(sketch, "E285.1.0.5", {"start": v(11.35, -3.3) * mm, "end": v(8.5, -1.65) * mm});
            skLineSegment(sketch, "E285.1.0.6", {"start": v(8.5, -1.65) * mm, "end": v(8.5, 1.65) * mm});
            skLineSegment(sketch, "E285.1.0.7", {"start": v(8.5, 1.65) * mm, "end": v(11.35, 3.3) * mm});
            skLineSegment(sketch, "E285.1.0.8", {"start": v(11.35, 3.3) * mm, "end": v(14.2, 1.65) * mm});
            skCircle(sketch, "E285.1.1.0", {"center": v(11.35, -41.3) * mm, "radius": 4.5 * mm});
            skPoint(sketch, "E285.1.1.1", {"position": v(14.2, -41.3) * mm});
            skCircle(sketch, "E285.1.1.2", {"center": v(11.35, -41.3) * mm, "radius": 2.85 * mm, "construction": true});
            skLineSegment(sketch, "E285.1.1.3", {"start": v(14.2, -39.65) * mm, "end": v(14.2, -42.95) * mm});
            skLineSegment(sketch, "E285.1.1.4", {"start": v(14.2, -42.95) * mm, "end": v(11.35, -44.6) * mm});
            skLineSegment(sketch, "E285.1.1.5", {"start": v(11.35, -44.6) * mm, "end": v(8.5, -42.95) * mm});
            skLineSegment(sketch, "E285.1.1.6", {"start": v(8.5, -42.95) * mm, "end": v(8.5, -39.65) * mm});
            skLineSegment(sketch, "E285.1.1.7", {"start": v(8.5, -39.65) * mm, "end": v(11.35, -38) * mm});
            skLineSegment(sketch, "E285.1.1.8", {"start": v(11.35, -38) * mm, "end": v(14.2, -39.65) * mm});
            skLineSegment(sketch, "E285.direction1", {"start": v(-14.2, -1.65) * mm, "end": v(8.5, -1.65) * mm, "construction": true});
            skLineSegment(sketch, "E285.direction2", {"start": v(-14.2, -1.65) * mm, "end": v(-14.2, -42.95) * mm, "construction": true});
            skLineSegment(sketch, "E286.0", {"start": v(17.05, -41.64) * mm, "end": v(16.77, -42.11) * mm});
            skLineSegment(sketch, "E286.1", {"start": v(17.43, -40.96) * mm, "end": v(17.05, -41.64) * mm});
            skLineSegment(sketch, "E286.2", {"start": v(17.78, -40.27) * mm, "end": v(17.43, -40.96) * mm});
            skLineSegment(sketch, "E286.3", {"start": v(18.11, -39.58) * mm, "end": v(17.78, -40.27) * mm});
            skLineSegment(sketch, "E286.4", {"start": v(18.42, -38.88) * mm, "end": v(18.11, -39.58) * mm});
            skLineSegment(sketch, "E286.5", {"start": v(18.71, -38.18) * mm, "end": v(18.42, -38.88) * mm});
            skLineSegment(sketch, "E286.6", {"start": v(18.99, -37.48) * mm, "end": v(18.71, -38.18) * mm});
            skLineSegment(sketch, "E286.7", {"start": v(19.24, -36.77) * mm, "end": v(18.99, -37.48) * mm});
            skLineSegment(sketch, "E286.8", {"start": v(21.3, -15.2) * mm, "end": v(21.36, -15.97) * mm});
            skLineSegment(sketch, "E286.9", {"start": v(21.24, -14.4) * mm, "end": v(21.3, -15.2) * mm});
            skLineSegment(sketch, "E286.10", {"start": v(21.16, -13.61) * mm, "end": v(21.24, -14.4) * mm});
            skLineSegment(sketch, "E286.11", {"start": v(21.07, -12.81) * mm, "end": v(21.16, -13.61) * mm});
            skLineSegment(sketch, "E286.12", {"start": v(20.97, -12) * mm, "end": v(21.07, -12.81) * mm});
            skLineSegment(sketch, "E286.13", {"start": v(20.85, -11.2) * mm, "end": v(20.97, -12) * mm});
            skLineSegment(sketch, "E286.14", {"start": v(20.72, -10.39) * mm, "end": v(20.85, -11.2) * mm});
            skLineSegment(sketch, "E286.15", {"start": v(20.57, -9.57) * mm, "end": v(20.72, -10.39) * mm});
            skLineSegment(sketch, "E286.16", {"start": v(20.41, -8.75) * mm, "end": v(20.57, -9.57) * mm});
            skLineSegment(sketch, "E286.17", {"start": v(20.24, -7.93) * mm, "end": v(20.41, -8.75) * mm});
            skLineSegment(sketch, "E286.18", {"start": v(20.04, -7.11) * mm, "end": v(20.24, -7.93) * mm});
            skLineSegment(sketch, "E286.19", {"start": v(19.83, -6.3) * mm, "end": v(20.04, -7.11) * mm});
            skLineSegment(sketch, "E286.20", {"start": v(17.76, -0.62) * mm, "end": v(18.12, -1.42) * mm});
            skLineSegment(sketch, "E286.21", {"start": v(17.37, 0.17) * mm, "end": v(17.76, -0.62) * mm});
            skLineSegment(sketch, "E286.22", {"start": v(16.96, 0.96) * mm, "end": v(17.37, 0.17) * mm});
            skLineSegment(sketch, "E286.23", {"start": v(16.88, 1.1) * mm, "end": v(16.96, 0.96) * mm});
            skLineSegment(sketch, "E286.24", {"start": v(18.12, -1.42) * mm, "end": v(18.46, -2.22) * mm});
            skLineSegment(sketch, "E286.25", {"start": v(18.46, -2.22) * mm, "end": v(18.78, -3.03) * mm});
            skLineSegment(sketch, "E286.26", {"start": v(18.78, -3.03) * mm, "end": v(19.07, -3.84) * mm});
            skLineSegment(sketch, "E286.27", {"start": v(19.07, -3.84) * mm, "end": v(19.34, -4.65) * mm});
            skLineSegment(sketch, "E286.28", {"start": v(19.34, -4.65) * mm, "end": v(19.6, -5.47) * mm});
            skLineSegment(sketch, "E286.29", {"start": v(19.6, -5.47) * mm, "end": v(19.83, -6.3) * mm});
            skLineSegment(sketch, "E286.30", {"start": v(21.36, -15.97) * mm, "end": v(21.4, -16.74) * mm});
            skLineSegment(sketch, "E286.31", {"start": v(21.4, -16.74) * mm, "end": v(21.45, -17.51) * mm});
            skLineSegment(sketch, "E286.32", {"start": v(21.45, -17.51) * mm, "end": v(21.5, -19) * mm});
            skLineSegment(sketch, "E286.33", {"start": v(21.5, -19) * mm, "end": v(21.52, -20.45) * mm});
            skLineSegment(sketch, "E286.34", {"start": v(21.52, -20.45) * mm, "end": v(21.52, -21.86) * mm});
            skLineSegment(sketch, "E286.35", {"start": v(21.52, -21.86) * mm, "end": v(21.5, -23.08) * mm});
            skLineSegment(sketch, "E286.36", {"start": v(21.5, -23.08) * mm, "end": v(21.45, -24.34) * mm});
            skLineSegment(sketch, "E286.37", {"start": v(21.45, -24.34) * mm, "end": v(21.37, -25.63) * mm});
            skLineSegment(sketch, "E286.38", {"start": v(21.37, -25.63) * mm, "end": v(21.32, -26.3) * mm});
            skLineSegment(sketch, "E286.39", {"start": v(21.32, -26.3) * mm, "end": v(21.27, -26.97) * mm});
            skLineSegment(sketch, "E286.40", {"start": v(21.27, -26.97) * mm, "end": v(21.2, -27.64) * mm});
            skLineSegment(sketch, "E286.41", {"start": v(21.2, -27.64) * mm, "end": v(21.12, -28.33) * mm});
            skLineSegment(sketch, "E286.42", {"start": v(21.12, -28.33) * mm, "end": v(21.04, -29.01) * mm});
            skLineSegment(sketch, "E286.43", {"start": v(21.04, -29.01) * mm, "end": v(20.94, -29.7) * mm});
            skLineSegment(sketch, "E286.44", {"start": v(20.94, -29.7) * mm, "end": v(20.83, -30.4) * mm});
            skLineSegment(sketch, "E286.45", {"start": v(20.83, -30.4) * mm, "end": v(20.7, -31.1) * mm});
            skLineSegment(sketch, "E286.46", {"start": v(20.7, -31.1) * mm, "end": v(20.58, -31.8) * mm});
            skLineSegment(sketch, "E286.47", {"start": v(20.58, -31.8) * mm, "end": v(20.43, -32.52) * mm});
            skLineSegment(sketch, "E286.48", {"start": v(20.43, -32.52) * mm, "end": v(20.27, -33.22) * mm});
            skLineSegment(sketch, "E286.49", {"start": v(20.27, -33.22) * mm, "end": v(20.1, -33.93) * mm});
            skLineSegment(sketch, "E286.50", {"start": v(20.1, -33.93) * mm, "end": v(19.9, -34.64) * mm});
            skLineSegment(sketch, "E286.51", {"start": v(19.9, -34.64) * mm, "end": v(19.7, -35.36) * mm});
            skLineSegment(sketch, "E286.52", {"start": v(19.7, -35.36) * mm, "end": v(19.48, -36.06) * mm});
            skLineSegment(sketch, "E286.53", {"start": v(19.48, -36.06) * mm, "end": v(19.24, -36.77) * mm});
            skSolve(sketch);
        }
        {
            var Q0;
            {var subQ0=sQuery(id+"F0.wireOp",EDGE,"E1");var subQ1=makeQuery(id+"F0.imprint","INTERSECT",VERTEX,{"derivedFrom":[sQuery(id+"F0.wireOp",EDGE,"E0.bottom"),subQ0]});Q0=makeQuery(id+"F0.imprint","IMPRINT",FACE,{"disambiguationData":[TD([[makeQuery(id+"F0.imprint","IMPRINT",EDGE,{"disambiguationData":[TD([[subQ1,1.0]])],"derivedFrom":subQ0}),1.0]])]});}
            extrude(context, id + "F4", {"entities" : qUnion([Q0]), "operationType" : NewBodyOperationType.REMOVE, "endBound" : BoundingType.UP_TO_NEXT, "depth" : 25 * mm});
        }
        {
            var Q0;
            {var subQ0=sQuery(id+"F0.wireOp",EDGE,"E0.left");var subQ1=sQuery(id+"F0.wireOp",EDGE,"E0.bottom");var subQ2=makeQuery(id+"F0.imprint","INTERSECT",VERTEX,{"derivedFrom":[subQ1,subQ0]});Q0=makeQuery(id+"F0.imprint","IMPRINT",FACE,{"disambiguationData":[TD([[makeQuery(id+"F0.imprint","IMPRINT",EDGE,{"disambiguationData":[TD([[subQ2,-1.0]])],"derivedFrom":subQ1}),1.0]])]});}
            var Q1;
            {var subQ0=sQuery(id+"F0.wireOp",EDGE,"E0.right");var subQ1=sQuery(id+"F0.wireOp",EDGE,"E0.bottom");var subQ2=makeQuery(id+"F0.imprint","INTERSECT",VERTEX,{"derivedFrom":[subQ1,subQ0]});Q1=makeQuery(id+"F0.imprint","IMPRINT",FACE,{"disambiguationData":[TD([[makeQuery(id+"F0.imprint","IMPRINT",EDGE,{"disambiguationData":[TD([[subQ2,1.0]])],"derivedFrom":subQ1}),1.0]])]});}
            var Q2;
            {var subQ0=sQuery(id+"F0.wireOp",EDGE,"E0.right");var subQ1=sQuery(id+"F0.wireOp",EDGE,"E0.top");var subQ2=makeQuery(id+"F0.imprint","INTERSECT",VERTEX,{"derivedFrom":[subQ1,subQ0]});Q2=makeQuery(id+"F0.imprint","IMPRINT",FACE,{"disambiguationData":[TD([[makeQuery(id+"F0.imprint","IMPRINT",EDGE,{"disambiguationData":[TD([[subQ2,1.0]])],"derivedFrom":subQ1}),-1.0]])]});}
            var Q3;
            {var subQ0=sQuery(id+"F0.wireOp",EDGE,"E0.left");var subQ1=sQuery(id+"F0.wireOp",EDGE,"E0.top");var subQ2=makeQuery(id+"F0.imprint","INTERSECT",VERTEX,{"derivedFrom":[subQ1,subQ0]});Q3=makeQuery(id+"F0.imprint","IMPRINT",FACE,{"disambiguationData":[TD([[makeQuery(id+"F0.imprint","IMPRINT",EDGE,{"disambiguationData":[TD([[subQ2,-1.0]])],"derivedFrom":subQ1}),-1.0]])]});}
            extrude(context, id + "F5", {"entities" : qUnion([Q0, Q1, Q2, Q3]), "operationType" : NewBodyOperationType.REMOVE, "depth" : 2 * mm});
        }
        {
            var Q0;
            Q0=makeQuery(id+"F1.opExtrude","CAP_EDGE",EDGE,{"disambiguationData":[OSD([sQuery(id+"F0.wireOp",EDGE,"E2.right")])],"isStart":false});
            var Q1;
            Q1=makeQuery(id+"F1.opExtrude","CAP_EDGE",EDGE,{"disambiguationData":[OSD([sQuery(id+"F0.wireOp",EDGE,"E2.bottom")])],"isStart":false});
            var Q2;
            Q2=makeQuery(id+"F1.opExtrude","CAP_EDGE",EDGE,{"disambiguationData":[OSD([sQuery(id+"F0.wireOp",EDGE,"E2.left")])],"isStart":false});
            var Q3;
            Q3=makeQuery(id+"F1.opExtrude","CAP_EDGE",EDGE,{"disambiguationData":[OSD([sQuery(id+"F0.wireOp",EDGE,"E2.top")])],"isStart":false});
            var Q4;
            Q4=makeQuery(id+"F1.opExtrude","SWEPT_EDGE",EDGE,{"disambiguationData":[OSD([sQuery(id+"F0.wireOp",EDGE,"E2.bottom"),sQuery(id+"F0.wireOp",EDGE,"E2.right")])]});
            var Q5;
            Q5=makeQuery(id+"F1.opExtrude","SWEPT_EDGE",EDGE,{"disambiguationData":[OSD([sQuery(id+"F0.wireOp",EDGE,"E2.bottom"),sQuery(id+"F0.wireOp",EDGE,"E2.left")])]});
            var Q6;
            Q6=makeQuery(id+"F1.opExtrude","SWEPT_EDGE",EDGE,{"disambiguationData":[OSD([sQuery(id+"F0.wireOp",EDGE,"E2.top"),sQuery(id+"F0.wireOp",EDGE,"E2.right")])]});
            var Q7;
            Q7=makeQuery(id+"F1.opExtrude","SWEPT_EDGE",EDGE,{"disambiguationData":[OSD([sQuery(id+"F0.wireOp",EDGE,"E2.top"),sQuery(id+"F0.wireOp",EDGE,"E2.left")])]});
            fillet(context, id + "F6", {"entities" : qUnion([Q0, Q1, Q2, Q3, Q4, Q5, Q6, Q7]), "radius" : 2.5 * mm, "tangentPropagation" : true, "allowEdgeOverflow" : false});
        }
        {
            var Q0;
            Q0=makeQuery(id+"F1.opExtrude","SWEPT_BODY",BODY,{"disambiguationData":[OSD([sQuery(id+"F0.wireOp",EDGE,"E2.bottom"),sQuery(id+"F0.wireOp",EDGE,"E2.top"),sQuery(id+"F0.wireOp",EDGE,"E2.left"),sQuery(id+"F0.wireOp",EDGE,"E2.right")])]});
            var Q1;
            Q1=sQuery(id+"F2.wireOp",EDGE,"E3");
            transform(context, id + "F7", {"entities" : qUnion([Q0]), "transformType" : TransformType.ROTATION, "transformAxis" : qUnion([Q1]), "angle" : 45 * degree, "oppositeDirection" : true, "makeCopy" : false});
        }
        {
            var Q0;
            Q0=makeQuery(id+"F3.imprint","IMPRINT",FACE,{"disambiguationData":[TD([[makeQuery(id+"F3.imprint","IMPRINT",EDGE,{"derivedFrom":sQuery(id+"F3.wireOp",EDGE,"ad654f4e-130b-46fd-ad55-2420ef06e064.1.0.0")}),1.0]])]});
            var Q1;
            Q1=makeQuery(id+"F3.imprint","IMPRINT",FACE,{"disambiguationData":[TD([[makeQuery(id+"F3.imprint","IMPRINT",EDGE,{"derivedFrom":sQuery(id+"F3.wireOp",EDGE,"E4")}),1.0]])]});
            var Q2;
            Q2=makeQuery(id+"F6.opFillet","BLEND_FACE",FACE,{"disambiguationData":[OSD([sQuery(id+"F0.wireOp",EDGE,"E2.bottom")])]});
            extrude(context, id + "F8", {"entities" : qUnion([Q0, Q1]), "oppositeDirection" : true, "endBoundEntityFace" : qUnion([Q2]), "depth" : 11 * mm, "hasSecondDirection" : true, "secondDirectionOppositeDirection" : false, "secondDirectionDepth" : 6.5 * mm});
        }
        {
            var Q0;
            Q0=makeQuery(id+"F5.boolean.opBoolean","COPY",FACE,{"derivedFrom":makeQuery(id+"F5.opExtrude","CAP_FACE",FACE,{"disambiguationData":[OSD([sQuery(id+"F0.wireOp",EDGE,"E0.bottom"),sQuery(id+"F0.wireOp",EDGE,"E0.right"),sQuery(id+"F0.wireOp",EDGE,"E1")])],"isStart":false})});
            var sketch = newSketch(context, id + "F9", { "sketchPlane" : qUnion([Q0])});
            skLineSegment(sketch, "E287.bottom", {"start": v(-6.25, -6.5) * mm, "end": v(6.25, -6.5) * mm});
            skLineSegment(sketch, "E287.top", {"start": v(-6.25, 6.5) * mm, "end": v(6.25, 6.5) * mm});
            skLineSegment(sketch, "E287.left", {"start": v(-6.25, -6.5) * mm, "end": v(-6.25, 6.5) * mm});
            skLineSegment(sketch, "E287.right", {"start": v(6.25, -6.5) * mm, "end": v(6.25, 6.5) * mm});
            skPoint(sketch, "E287.middle", {"position": v(0, 0) * mm});
            skCircle(sketch, "E288", {"center": v(0, 0) * mm, "radius": 7.25 * mm});
            skSolve(sketch);
        }
        {
            var Q0;
            {var subQ1=sQuery(id+"F0.wireOp",EDGE,"E1");var subQ2=sQuery(id+"F0.wireOp",EDGE,"E0.bottom");var subQ4=makeQuery(id+"F5.boolean.opBoolean","COPY",EDGE,{"derivedFrom":makeQuery(id+"F5.opExtrude","CAP_EDGE",EDGE,{"disambiguationData":[OSD([subQ1]),TDD([makeQuery(id+"F0.imprint","IMPRINT",EDGE,{"disambiguationData":[TD([[makeQuery(id+"F0.imprint","INTERSECT",VERTEX,{"derivedFrom":[subQ2,subQ1]}),-1.0]])],"derivedFrom":subQ1})])],"isStart":false})});Q0=makeQuery(id+"F9.imprint","IMPRINT",FACE,{"disambiguationData":[TD([[makeQuery(id+"F9.imprint","IMPRINT",EDGE,{"derivedFrom":subQ4}),1.0]])]});}
            var Q1;
            {var subQ5=sQuery(id+"F9.wireOp",EDGE,"E287.top");Q1=makeQuery(id+"F9.imprint","IMPRINT",FACE,{"disambiguationData":[TD([[makeQuery(id+"F9.imprint","IMPRINT",EDGE,{"derivedFrom":subQ5}),-1.0]])]});}
            extrude(context, id + "F10", {"entities" : qUnion([Q0, Q1]), "operationType" : NewBodyOperationType.REMOVE, "depth" : 25 * mm});
        }
        {
            var Q0;
            Q0=qSketchRegion(id+"F9",true);
            extrude(context, id + "F11", {"entities" : qUnion([Q0]), "operationType" : NewBodyOperationType.REMOVE, "depth" : 25 * mm});
        }
        {
            var Q0;
            {var subQ0=sQuery(id+"F9.wireOp",EDGE,"E288");var subQ1=makeQuery(id+"F9.imprint","INTERSECT",VERTEX,{"derivedFrom":[sQuery(id+"F9.wireOp",EDGE,"E287.top"),subQ0]});var subQ2=makeQuery(id+"F9.imprint","INTERSECT",VERTEX,{"derivedFrom":[sQuery(id+"F9.wireOp",EDGE,"E287.right"),subQ0]});Q0=makeQuery(id+"F9.imprint","IMPRINT",FACE,{"disambiguationData":[TD([[makeQuery(id+"F9.imprint","IMPRINT",EDGE,{"disambiguationData":[TD([[subQ1,1.0],[subQ2,-1.0]])],"derivedFrom":subQ0}),1.0]])]});}
            extrude(context, id + "F12", {"entities" : qUnion([Q0]), "operationType" : NewBodyOperationType.REMOVE, "oppositeDirection" : true, "depth" : 25 * mm});
        }
        {
            var Q0;
            Q0=makeQuery(id+"F1.opExtrude","CAP_EDGE",EDGE,{"disambiguationData":[OSD([sQuery(id+"F0.wireOp",EDGE,"E2.bottom")])],"isStart":true});
            var Q1;
            Q1=makeQuery(id+"F1.opExtrude","CAP_EDGE",EDGE,{"disambiguationData":[OSD([sQuery(id+"F0.wireOp",EDGE,"E2.top")])],"isStart":true});
            fillet(context, id + "F13", {"entities" : qUnion([Q0, Q1]), "radius" : 1 * mm, "tangentPropagation" : true, "allowEdgeOverflow" : false});
        }
    });
